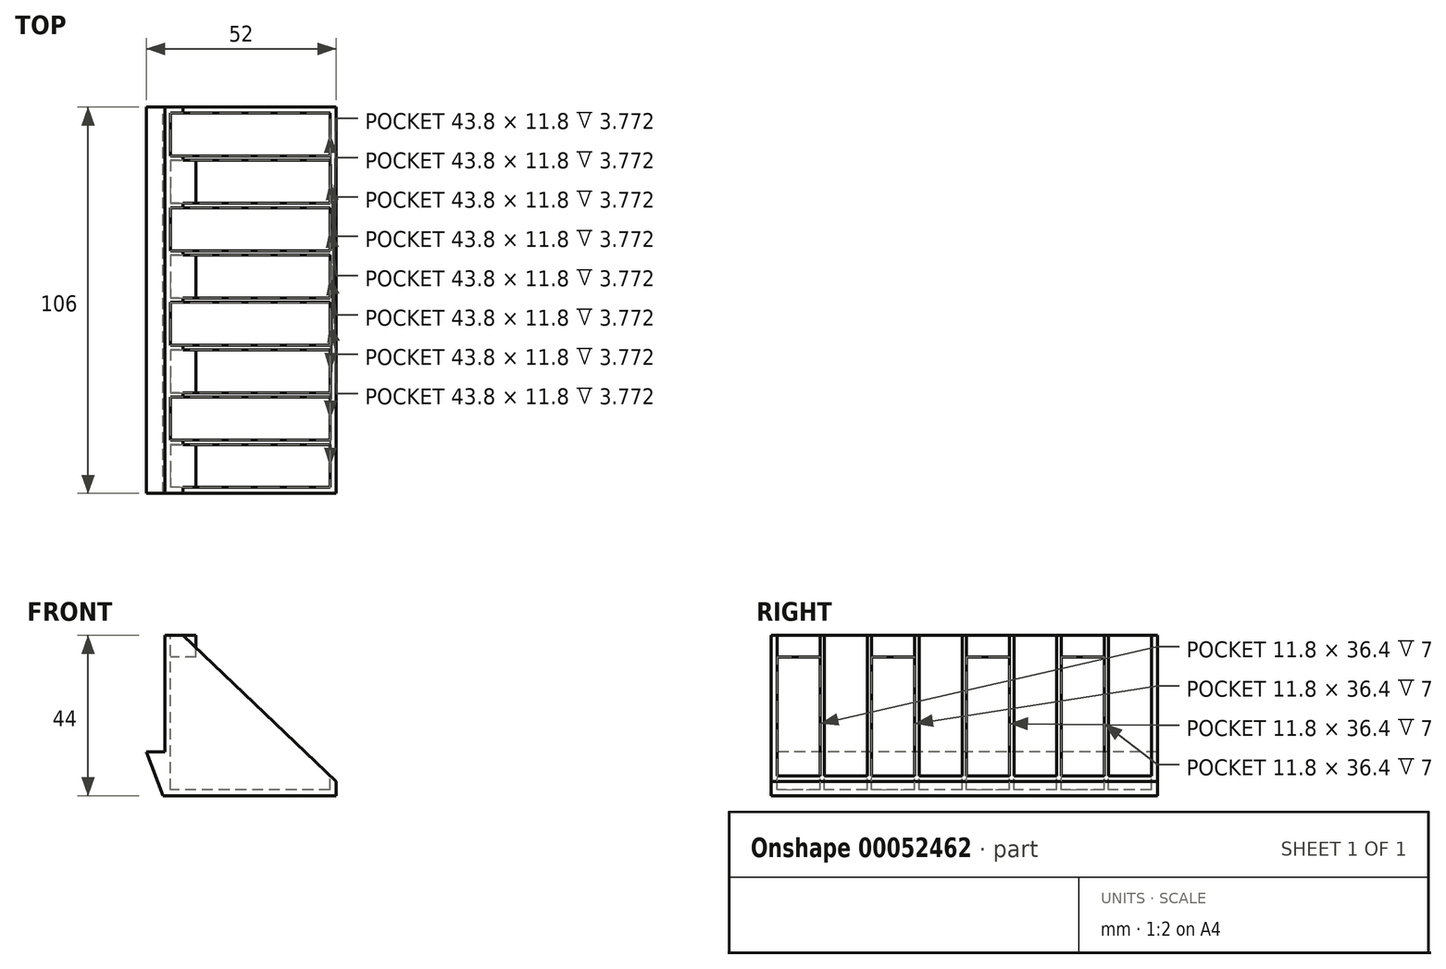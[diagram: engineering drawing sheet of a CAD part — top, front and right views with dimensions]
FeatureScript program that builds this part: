
annotation { "Feature Type Name" : "Feature", "Feature Type Description" : "" }
export const myFeature = defineFeature(function(context is Context, id is Id, definition is map)
    precondition{}
    {
        {
            var Q0;
            Q0=qCreatedBy(makeId("Right.planeOp"),FACE);
            var sketch = newSketch(context, id + "F0", { "sketchPlane" : qUnion([Q0])});
            skLineSegment(sketch, "E0.bottom", {"start": v(53, -22) * mm, "end": v(-53, -22) * mm});
            skLineSegment(sketch, "E0.top", {"start": v(53, 22) * mm, "end": v(-53, 22) * mm});
            skLineSegment(sketch, "E0.left", {"start": v(53, -22) * mm, "end": v(53, 22) * mm});
            skLineSegment(sketch, "E0.right", {"start": v(-53, -22) * mm, "end": v(-53, 22) * mm});
            skPoint(sketch, "E0.middle", {"position": v(0, 0) * mm});
            skLineSegment(sketch, "E1", {"start": v(0, 89.01) * mm, "end": v(0, -87.1) * mm, "construction": true});
            skLineSegment(sketch, "E2", {"start": v(-157.02, 0) * mm, "end": v(150.34, 0) * mm, "construction": true});
            skSolve(sketch);
        }
        {
            var Q0;
            Q0 = qSketchRegion(id + "F0", true);
            extrude(context, id + "F1", {"entities" : qUnion([Q0]), "depth" : 47 * mm});
        }
        {
            var Q0;
            Q0=makeQuery(id+"F1.opExtrude","SWEPT_FACE",FACE,{"disambiguationData":[OSD([sQuery(id+"F0.wireOp",EDGE,"E0.top")])]});
            shell(context, id + "F2", {"entities" : qUnion([Q0]), "thickness" : 1.6 * mm});
        }
        {
            var Q0;
            Q0=makeQuery(id+"F2.opShell","OFFSET_FACE",FACE,{"disambiguationData":[OSD([sQuery(id+"F0.wireOp",EDGE,"E0.bottom")])]});
            var sketch = newSketch(context, id + "F3", { "sketchPlane" : qUnion([Q0])});
            skPoint(sketch, "E3.startSnap0", {"position": v(23.5, -51.4) * mm});
            skPoint(sketch, "E3.endSnap0", {"position": v(23.5, 51.4) * mm});
            skLineSegment(sketch, "E4", {"start": v(-26.68, 0) * mm, "end": v(70.25, 0) * mm, "construction": true});
            skLineSegment(sketch, "E5", {"start": v(23.5, 55.92) * mm, "end": v(23.5, -54.36) * mm, "construction": true});
            skLineSegment(sketch, "E6.bottom", {"start": v(0, -0.6) * mm, "end": v(47, -0.6) * mm});
            skLineSegment(sketch, "E6.top", {"start": v(0, 0.6) * mm, "end": v(47, 0.6) * mm});
            skLineSegment(sketch, "E6.left", {"start": v(0, -0.6) * mm, "end": v(0, 0.6) * mm});
            skLineSegment(sketch, "E6.right", {"start": v(47, -0.6) * mm, "end": v(47, 0.6) * mm});
            skPoint(sketch, "E6.middle", {"position": v(23.5, 0) * mm});
            skLineSegment(sketch, "E7.bottom", {"start": v(0, 12.4) * mm, "end": v(46.58, 12.4) * mm});
            skLineSegment(sketch, "E7.top", {"start": v(0, 13.6) * mm, "end": v(46.58, 13.6) * mm});
            skLineSegment(sketch, "E7.left", {"start": v(0, 12.4) * mm, "end": v(0, 13.6) * mm});
            skLineSegment(sketch, "E7.right", {"start": v(46.58, 12.4) * mm, "end": v(46.58, 13.6) * mm});
            skLineSegment(sketch, "E8.bottom", {"start": v(0, 26.6) * mm, "end": v(46.58, 26.6) * mm});
            skLineSegment(sketch, "E8.top", {"start": v(0, 25.4) * mm, "end": v(46.58, 25.4) * mm});
            skLineSegment(sketch, "E8.left", {"start": v(0, 26.6) * mm, "end": v(0, 25.4) * mm});
            skLineSegment(sketch, "E8.right", {"start": v(46.58, 26.6) * mm, "end": v(46.58, 25.4) * mm});
            skLineSegment(sketch, "E9.bottom", {"start": v(0, 38.4) * mm, "end": v(46.58, 38.4) * mm});
            skLineSegment(sketch, "E9.top", {"start": v(0, 39.6) * mm, "end": v(46.58, 39.6) * mm});
            skLineSegment(sketch, "E9.left", {"start": v(0, 38.4) * mm, "end": v(0, 39.6) * mm});
            skLineSegment(sketch, "E9.right", {"start": v(46.58, 38.4) * mm, "end": v(46.58, 39.6) * mm});
            skLineSegment(sketch, "E10.MirrorCS", {"start": v(0, -12.4) * mm, "end": v(46.58, -12.4) * mm});
            skLineSegment(sketch, "E11.MirrorCS", {"start": v(0, -13.6) * mm, "end": v(46.58, -13.6) * mm});
            skLineSegment(sketch, "E12.MirrorCS", {"start": v(0, -26.6) * mm, "end": v(46.58, -26.6) * mm});
            skLineSegment(sketch, "E13.MirrorCS", {"start": v(0, -25.4) * mm, "end": v(46.58, -25.4) * mm});
            skLineSegment(sketch, "E14.MirrorCS", {"start": v(0, -38.4) * mm, "end": v(46.58, -38.4) * mm});
            skLineSegment(sketch, "E15.MirrorCS", {"start": v(0, -39.6) * mm, "end": v(46.58, -39.6) * mm});
            skLineSegment(sketch, "E16.MirrorCS", {"start": v(46.58, -12.4) * mm, "end": v(46.58, -13.6) * mm});
            skLineSegment(sketch, "E17.MirrorCS", {"start": v(46.58, -26.6) * mm, "end": v(46.58, -25.4) * mm});
            skLineSegment(sketch, "E18.MirrorCS", {"start": v(46.58, -38.4) * mm, "end": v(46.58, -39.6) * mm});
            skLineSegment(sketch, "E19.MirrorCS", {"start": v(0, -38.4) * mm, "end": v(0, -39.6) * mm});
            skLineSegment(sketch, "E20.MirrorCS", {"start": v(0, -26.6) * mm, "end": v(0, -25.4) * mm});
            skLineSegment(sketch, "E21.MirrorCS", {"start": v(0, -12.4) * mm, "end": v(0, -13.6) * mm});
            skSolve(sketch);
        }
        {
            var Q0;
            Q0 = qSketchRegion(id + "F3", true);
            extrude(context, id + "F4", {"entities" : qUnion([Q0]), "operationType" : NewBodyOperationType.ADD, "depth" : 42.4 * mm});
        }
        {
            var Q0;
            Q0=makeQuery(id+"F1.opExtrude","SWEPT_FACE",FACE,{"disambiguationData":[OSD([sQuery(id+"F0.wireOp",EDGE,"E0.left")])]});
            var sketch = newSketch(context, id + "F5", { "sketchPlane" : qUnion([Q0])});
            skLineSegment(sketch, "E22", {"start": v(-47, 22) * mm, "end": v(-5, 22) * mm});
            skLineSegment(sketch, "E23", {"start": v(-5, 22) * mm, "end": v(-47, -18.16) * mm});
            skLineSegment(sketch, "E24", {"start": v(-47, -18.16) * mm, "end": v(-47, 22) * mm});
            skSolve(sketch);
        }
        {
            var Q0;
            Q0 = qSketchRegion(id + "F5", true);
            extrude(context, id + "F6", {"entities" : qUnion([Q0]), "operationType" : NewBodyOperationType.REMOVE, "oppositeDirection" : true, "depth" : 143 * mm});
        }
        {
            var Q0;
            {var subQ0=sQuery(id+"F0.wireOp",EDGE,"E0.bottom");var subQ1=sQuery(id+"F0.wireOp",EDGE,"E0.top");var subQ3=sQuery(id+"F3.wireOp",EDGE,"E8.bottom");var subQ4=sQuery(id+"F0.wireOp",EDGE,"E0.right");var subQ5=sQuery(id+"F0.wireOp",EDGE,"E0.left");Q0=makeQuery(id+"F4.boolean.opBoolean","SPLIT",FACE,{"disambiguationData":[TD([makeQuery(id+"F4.opExtrude","SWEPT_FACE",FACE,{"disambiguationData":[OSD([subQ3])]})])],"derivedFrom":makeQuery(id+"F2.opShell","OFFSET_FACE",FACE,{"disambiguationData":[OSD([subQ0,subQ1,subQ5,subQ4]),TDD([makeQuery(id+"F1.opExtrude","CAP_FACE",FACE,{"disambiguationData":[OSD([subQ0,subQ1,subQ5,subQ4])],"isStart":true})])]})});}
            var sketch = newSketch(context, id + "F7", { "sketchPlane" : qUnion([Q0])});
            skLineSegment(sketch, "E25.bottom", {"start": v(38.4, 22) * mm, "end": v(26.6, 22) * mm});
            skLineSegment(sketch, "E25.top", {"start": v(38.4, 16) * mm, "end": v(26.6, 16) * mm});
            skLineSegment(sketch, "E25.left", {"start": v(38.4, 22) * mm, "end": v(38.4, 16) * mm});
            skLineSegment(sketch, "E25.right", {"start": v(26.6, 22) * mm, "end": v(26.6, 16) * mm});
            skSolve(sketch);
        }
        {
            var Q0;
            Q0 = qSketchRegion(id + "F7", true);
            extrude(context, id + "F8", {"entities" : qUnion([Q0]), "operationType" : NewBodyOperationType.ADD, "depth" : 7 * mm});
        }
        {
            var Q0;
            Q0=makeQuery(id+"F1.opExtrude","CAP_FACE",FACE,{"disambiguationData":[OSD([sQuery(id+"F0.wireOp",EDGE,"E0.bottom"),sQuery(id+"F0.wireOp",EDGE,"E0.top"),sQuery(id+"F0.wireOp",EDGE,"E0.left"),sQuery(id+"F0.wireOp",EDGE,"E0.right")])],"isStart":true});
            var sketch = newSketch(context, id + "F9", { "sketchPlane" : qUnion([Q0])});
            skLineSegment(sketch, "E26", {"start": v(0, -24.88) * mm, "end": v(0, 4.62) * mm, "construction": true});
            skPoint(sketch, "E26.startSnap0", {"position": v(0, -22) * mm});
            skLineSegment(sketch, "E27.MirrorCS", {"start": v(-8.87, -22) * mm, "end": v(-3.87, -22) * mm});
            skLineSegment(sketch, "E28.bottom", {"start": v(-53, -22) * mm, "end": v(53, -22) * mm});
            skLineSegment(sketch, "E28.top", {"start": v(-53, -10) * mm, "end": v(53, -10) * mm});
            skLineSegment(sketch, "E28.left", {"start": v(-53, -22) * mm, "end": v(-53, -10) * mm});
            skLineSegment(sketch, "E28.right", {"start": v(53, -22) * mm, "end": v(53, -10) * mm});
            skSolve(sketch);
        }
        {
            var Q0;
            Q0 = qSketchRegion(id + "F9", true);
            extrude(context, id + "F10", {"entities" : qUnion([Q0]), "operationType" : NewBodyOperationType.ADD, "depth" : 5 * mm});
        }
        {
            var Q0;
            {var subQ1=sQuery(id+"F3.wireOp",EDGE,"E7.bottom");var subQ2=sQuery(id+"F0.wireOp",EDGE,"E0.bottom");var subQ3=sQuery(id+"F0.wireOp",EDGE,"E0.top");var subQ4=sQuery(id+"F0.wireOp",EDGE,"E0.right");var subQ5=sQuery(id+"F0.wireOp",EDGE,"E0.left");Q0=makeQuery(id+"F4.boolean.opBoolean","SPLIT",FACE,{"disambiguationData":[TD([makeQuery(id+"F4.opExtrude","SWEPT_FACE",FACE,{"disambiguationData":[OSD([subQ1])]})])],"derivedFrom":makeQuery(id+"F2.opShell","OFFSET_FACE",FACE,{"disambiguationData":[OSD([subQ2,subQ3,subQ5,subQ4]),TDD([makeQuery(id+"F1.opExtrude","CAP_FACE",FACE,{"disambiguationData":[OSD([subQ2,subQ3,subQ5,subQ4])],"isStart":true})])]})});}
            var sketch = newSketch(context, id + "F11", { "sketchPlane" : qUnion([Q0])});
            skLineSegment(sketch, "E29.bottom", {"start": v(12.4, 22) * mm, "end": v(0.6, 22) * mm});
            skLineSegment(sketch, "E29.top", {"start": v(12.4, 16) * mm, "end": v(0.6, 16) * mm});
            skLineSegment(sketch, "E29.left", {"start": v(12.4, 22) * mm, "end": v(12.4, 16) * mm});
            skLineSegment(sketch, "E29.right", {"start": v(0.6, 22) * mm, "end": v(0.6, 16) * mm});
            skSolve(sketch);
        }
        {
            var Q0;
            Q0 = qSketchRegion(id + "F11", true);
            extrude(context, id + "F12", {"entities" : qUnion([Q0]), "operationType" : NewBodyOperationType.ADD, "depth" : 7 * mm});
        }
        {
            var Q0;
            {var subQ0=sQuery(id+"F3.wireOp",EDGE,"E11.MirrorCS");var subQ2=sQuery(id+"F0.wireOp",EDGE,"E0.bottom");var subQ3=sQuery(id+"F0.wireOp",EDGE,"E0.top");var subQ4=sQuery(id+"F0.wireOp",EDGE,"E0.right");var subQ5=sQuery(id+"F0.wireOp",EDGE,"E0.left");Q0=makeQuery(id+"F4.boolean.opBoolean","SPLIT",FACE,{"disambiguationData":[TD([makeQuery(id+"F4.opExtrude","SWEPT_FACE",FACE,{"disambiguationData":[OSD([subQ0])]})])],"derivedFrom":makeQuery(id+"F2.opShell","OFFSET_FACE",FACE,{"disambiguationData":[OSD([subQ2,subQ3,subQ5,subQ4]),TDD([makeQuery(id+"F1.opExtrude","CAP_FACE",FACE,{"disambiguationData":[OSD([subQ2,subQ3,subQ5,subQ4])],"isStart":true})])]})});}
            var sketch = newSketch(context, id + "F13", { "sketchPlane" : qUnion([Q0])});
            skLineSegment(sketch, "E30.bottom", {"start": v(-13.6, 22) * mm, "end": v(-25.4, 22) * mm});
            skLineSegment(sketch, "E30.top", {"start": v(-13.6, 16) * mm, "end": v(-25.4, 16) * mm});
            skLineSegment(sketch, "E30.left", {"start": v(-13.6, 22) * mm, "end": v(-13.6, 16) * mm});
            skLineSegment(sketch, "E30.right", {"start": v(-25.4, 22) * mm, "end": v(-25.4, 16) * mm});
            skSolve(sketch);
        }
        {
            var Q0;
            Q0 = qSketchRegion(id + "F13", true);
            extrude(context, id + "F14", {"entities" : qUnion([Q0]), "operationType" : NewBodyOperationType.ADD, "depth" : 7 * mm});
        }
        {
            var Q0;
            {var subQ1=sQuery(id+"F0.wireOp",EDGE,"E0.bottom");var subQ2=sQuery(id+"F0.wireOp",EDGE,"E0.top");var subQ3=sQuery(id+"F0.wireOp",EDGE,"E0.right");var subQ4=sQuery(id+"F0.wireOp",EDGE,"E0.left");Q0=makeQuery(id+"F4.boolean.opBoolean","SPLIT",FACE,{"disambiguationData":[TD([makeQuery(id+"F2.opShell","OFFSET_FACE",FACE,{"disambiguationData":[OSD([subQ3])]})])],"derivedFrom":makeQuery(id+"F2.opShell","OFFSET_FACE",FACE,{"disambiguationData":[OSD([subQ1,subQ2,subQ4,subQ3]),TDD([makeQuery(id+"F1.opExtrude","CAP_FACE",FACE,{"disambiguationData":[OSD([subQ1,subQ2,subQ4,subQ3])],"isStart":true})])]})});}
            var sketch = newSketch(context, id + "F15", { "sketchPlane" : qUnion([Q0])});
            skLineSegment(sketch, "E31.bottom", {"start": v(-39.6, 22) * mm, "end": v(-51.4, 22) * mm});
            skLineSegment(sketch, "E31.top", {"start": v(-39.6, 16) * mm, "end": v(-51.4, 16) * mm});
            skLineSegment(sketch, "E31.left", {"start": v(-39.6, 22) * mm, "end": v(-39.6, 16) * mm});
            skLineSegment(sketch, "E31.right", {"start": v(-51.4, 22) * mm, "end": v(-51.4, 16) * mm});
            skSolve(sketch);
        }
        {
            var Q0;
            Q0 = qSketchRegion(id + "F15", true);
            extrude(context, id + "F16", {"entities" : qUnion([Q0]), "operationType" : NewBodyOperationType.ADD, "depth" : 7 * mm});
        }
        {
            var Q0;
            Q0=makeQuery(id+"F10.boolean.opBoolean","MERGE",FACE,{"derivedFrom":[makeQuery(id+"F1.opExtrude","SWEPT_FACE",FACE,{"disambiguationData":[OSD([sQuery(id+"F0.wireOp",EDGE,"E0.left")])]}),makeQuery(id+"F10.opExtrude","SWEPT_FACE",FACE,{"disambiguationData":[OSD([sQuery(id+"F9.wireOp",EDGE,"E28.left")])]})]});
            var sketch = newSketch(context, id + "F17", { "sketchPlane" : qUnion([Q0])});
            skLineSegment(sketch, "E32", {"start": v(5, -10) * mm, "end": v(5, -22) * mm});
            skLineSegment(sketch, "E33", {"start": v(5, -22) * mm, "end": v(0.4, -22) * mm});
            skLineSegment(sketch, "E34", {"start": v(0.4, -22) * mm, "end": v(5, -10) * mm});
            skSolve(sketch);
        }
        {
            var Q0;
            Q0 = qSketchRegion(id + "F17", true);
            extrude(context, id + "F18", {"entities" : qUnion([Q0]), "operationType" : NewBodyOperationType.REMOVE, "oppositeDirection" : true, "depth" : 119 * mm});
        }
    });
